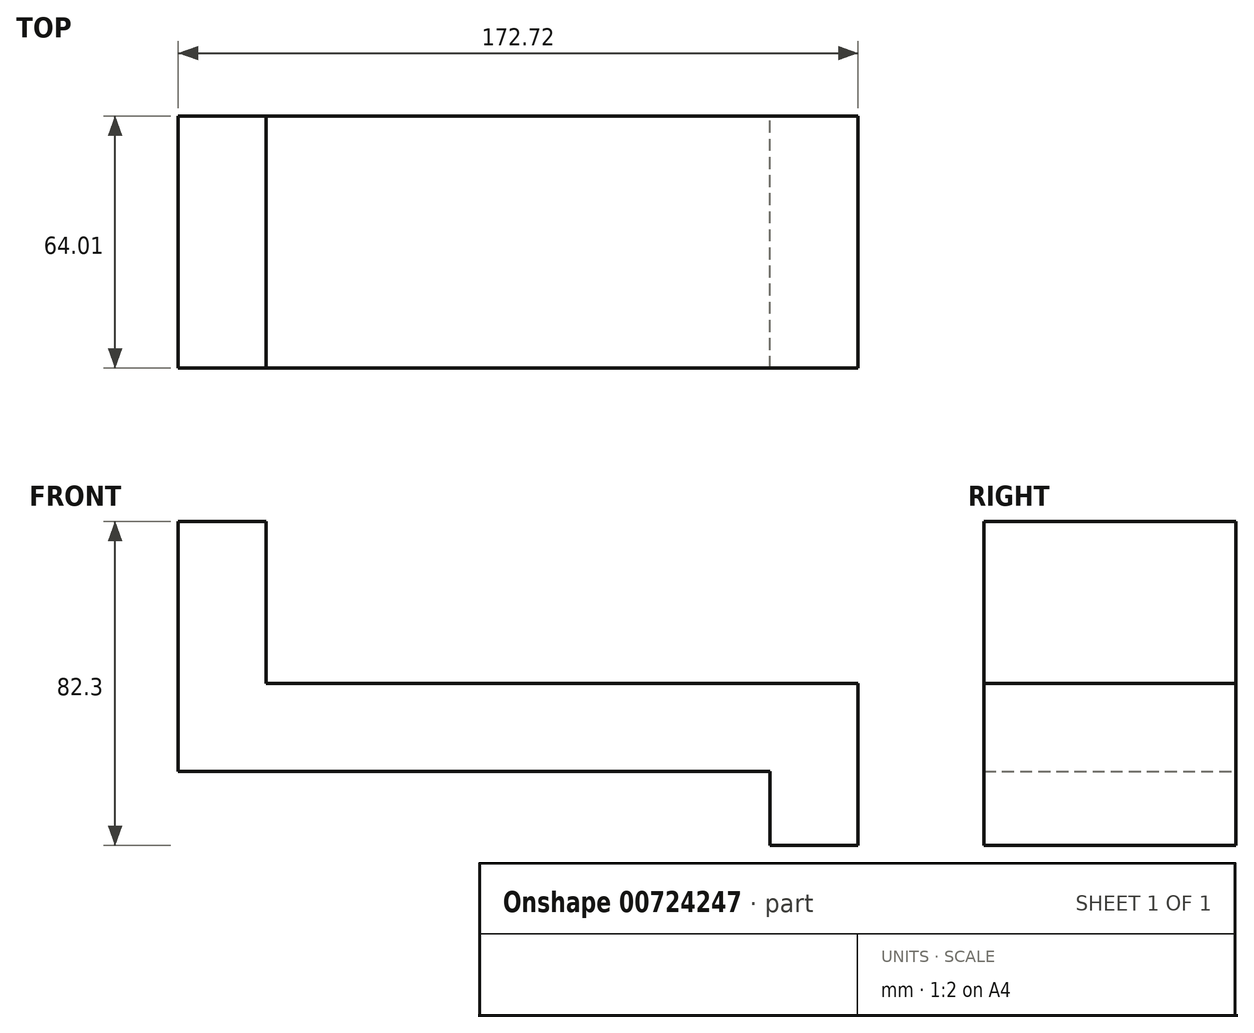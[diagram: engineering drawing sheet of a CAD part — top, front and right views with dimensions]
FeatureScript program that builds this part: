
annotation { "Feature Type Name" : "Feature", "Feature Type Description" : "" }
export const myFeature = defineFeature(function(context is Context, id is Id, definition is map)
    precondition{}
    {
        {
            var Q0;
            Q0=qCreatedBy(makeId("Front.planeOp"),FACE);
            var sketch = newSketch(context, id + "F0", { "sketchPlane" : qUnion([Q0])});
            skLineSegment(sketch, "E0", {"start": v(-76.01, 82.3) * mm, "end": v(-76.01, 18.8) * mm});
            skLineSegment(sketch, "E1", {"start": v(-76.01, 18.8) * mm, "end": v(74.35, 18.8) * mm});
            skLineSegment(sketch, "E2", {"start": v(74.35, 18.8) * mm, "end": v(74.35, 0) * mm});
            skLineSegment(sketch, "E3", {"start": v(74.35, 0) * mm, "end": v(96.7, 0) * mm});
            skLineSegment(sketch, "E4", {"start": v(96.7, 0) * mm, "end": v(96.7, 41.15) * mm});
            skLineSegment(sketch, "E5", {"start": v(96.7, 41.15) * mm, "end": v(-53.66, 41.15) * mm});
            skLineSegment(sketch, "E6", {"start": v(-53.66, 41.15) * mm, "end": v(-53.66, 82.3) * mm});
            skLineSegment(sketch, "E7", {"start": v(-53.66, 82.3) * mm, "end": v(-76.01, 82.3) * mm});
            skSolve(sketch);
        }
        {
            var Q0;
            Q0=makeQuery(id+"F0.imprint","IMPRINT",FACE,{"disambiguationData":[TD([[makeQuery(id+"F0.imprint","IMPRINT",EDGE,{"derivedFrom":sQuery(id+"F0.wireOp",EDGE,"E0")}),1.0]])]});
            extrude(context, id + "F1", {"entities" : qUnion([Q0]), "depth" : 64 * mm, "offsetDistance" : 25.4 * mm});
        }
    });
